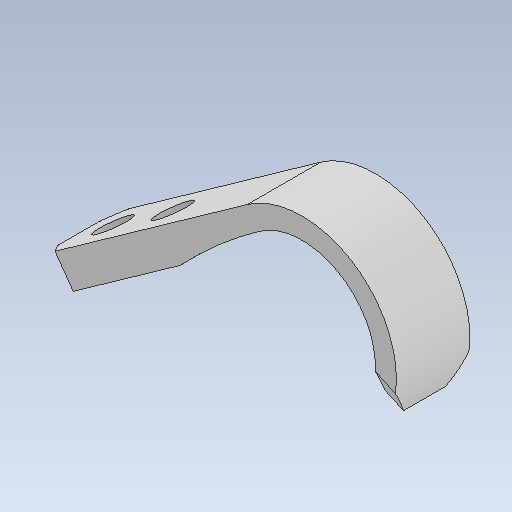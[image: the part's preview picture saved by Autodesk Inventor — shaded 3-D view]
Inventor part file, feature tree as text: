
AUTODESK INVENTOR PART (.ipt)
format: ipt  version: 2023 (Build 270158000, 158)  size: 124,416 bytes
history: native  units: mm
features: other x3, sketch x3, plane x1
ambient origin geometry x8: Origin, YZ Plane, XZ Plane, XY Plane, X Axis, Y Axis, Z Axis, Center Point
bodies: Solid1 (feature_tree)
feature tree (7):
  other  "foot_2.ipt"
  other  "Solid1::foot_2.ipt"
  other  "TaggingFeature1"
  sketch  "Sketch1"  dims[d0=10.0mm]
  sketch  "Sketch2"
  sketch  "Sketch3"
  plane  "Work Plane1"
